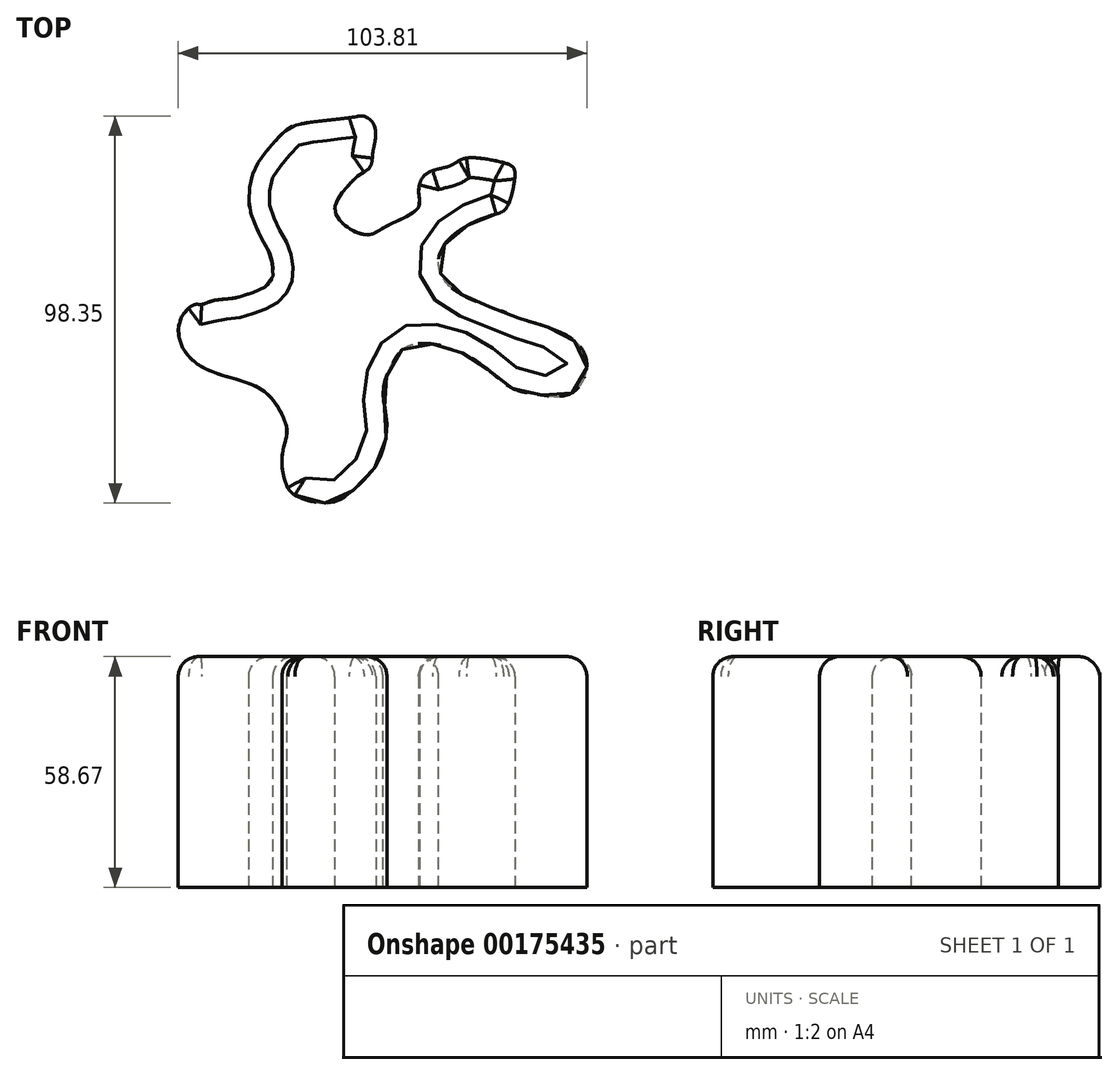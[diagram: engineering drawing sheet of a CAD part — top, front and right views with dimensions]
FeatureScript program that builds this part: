
annotation { "Feature Type Name" : "Feature", "Feature Type Description" : "" }
export const myFeature = defineFeature(function(context is Context, id is Id, definition is map)
    precondition{}
    {
        {
            var Q0;
            Q0=qCreatedBy(makeId("Top.planeOp"),FACE);
            var sketch = newSketch(context, id + "F0", { "sketchPlane" : qUnion([Q0])});
            skFitSpline(sketch, "E0", {"points": [v(-16.93, 51.2) * mm, v(-29.83, 49.58) * mm, v(-33.86, 47.76) * mm, v(-39.9, 40.91) * mm, v(-42.32, 36.28) * mm, v(-43.13, 30.43) * mm, v(-42.73, 27) * mm, v(-41.92, 24.79) * mm, v(-39.7, 19.95) * mm, v(-37.89, 16.73) * mm, v(-37.08, 13.5) * mm, v(-37.28, 10.08) * mm, v(-40.1, 7.46) * mm, v(-44.14, 6.05) * mm, v(-46.76, 5.24) * mm, v(-52.2, 4.64) * mm, v(-55.22, 3.63) * mm, v(-56.83, 3.63) * mm, v(-60.46, 0) * mm, v(-60.26, -6.65) * mm, v(-53.81, -12.9) * mm, v(-40.3, -17.74) * mm, v(-34.87, -23.98) * mm, v(-33.46, -28.82) * mm, v(-34.66, -34.66) * mm, v(-33.46, -42.52) * mm, v(-30.43, -45.35) * mm, v(-22.57, -46.76) * mm, v(-17.33, -44.14) * mm, v(-13.3, -40.3) * mm, v(-10.08, -35.87) * mm, v(-8.06, -26.6) * mm, v(-9.07, -18.54) * mm, v(-6.65, -11.29) * mm, v(-2.02, -6.65) * mm, v(12.7, -9.47) * mm, v(23.18, -17.33) * mm, v(29.83, -19.15) * mm, v(38.7, -18.94) * mm, v(42.73, -11.9) * mm, v(38.3, -4.64) * mm, v(26, 0) * mm, v(21.56, 1.81) * mm, v(7.26, 8.87) * mm, v(6.45, 18.74) * mm, v(18.14, 26.2) * mm, v(22.17, 28.01) * mm, v(24.39, 35.47) * mm, v(23.98, 38.5) * mm, v(19.75, 40.1) * mm, v(11.49, 40.71) * mm, v(8.06, 38.9) * mm, v(2.02, 36.88) * mm, v(0, 32.45) * mm, v(0, 28.42) * mm, v(-5.64, 24.79) * mm, v(-9.88, 22.57) * mm, v(-13.7, 21.36) * mm, v(-21.16, 26.8) * mm, v(-18.74, 32.85) * mm, v(-15.12, 36.48) * mm, v(-12.3, 38.7) * mm, v(-11.69, 41.92) * mm, v(-11.08, 45.14) * mm, v(-11.29, 49.17) * mm, v(-13.7, 51.4) * mm, v(-16.93, 51.2) * mm]});
            skSolve(sketch);
        }
        {
            var Q0;
            Q0=makeQuery(id+"F0.imprint","IMPRINT",FACE,{"disambiguationData":[TD([[makeQuery(id+"F0.imprint","IMPRINT",EDGE,{"derivedFrom":sQuery(id+"F0.wireOp",EDGE,"E0")}),1.0]])]});
            extrude(context, id + "F1", {"entities" : qUnion([Q0]), "depth" : 58.67 * mm});
        }
        {
            var Q0;
            Q0=makeQuery(id+"F1.opExtrude","CAP_EDGE",EDGE,{"disambiguationData":[OSD([sQuery(id+"F0.wireOp",EDGE,"E0")])],"isStart":false});
            fillet(context, id + "F2", {"entities" : qUnion([Q0]), "radius" : 5.08 * mm, "tangentPropagation" : true, "allowEdgeOverflow" : false});
        }
    });
